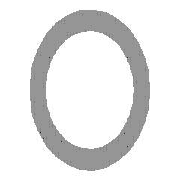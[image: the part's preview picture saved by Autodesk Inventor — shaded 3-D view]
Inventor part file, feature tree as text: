
AUTODESK INVENTOR PART (.ipt)
format: ipt  version: 2013 (Build 170138000, 138)  size: 109,568 bytes
history: native  units: mm (DEFAULTED — no unit token found)
features: other x4, sketch x3, plane x1
ambient origin geometry x8: Origin, YZ Plane, XZ Plane, XY Plane, X Axis, Y Axis, Z Axis, Center Point
bodies: Solid1 (feature_tree), Body (feature_tree)
feature tree (8):
  parser-record x1  (decoder bookkeeping rows leaked as tree rows — omitted from the tree; the rows remain in map.json)
  other  "Driven Length"
  other  "Start plane"
  other  "End plane"
  sketch  "Sketch"  dims[d2=365.252mm d3=0.0mm d4=-0.0mm d5=365.252mm d6=90.0deg d7=365.252mm]
  sketch  "Sketch3"  dims[d0=42.164mm]
  plane  "Work Plane3"
  sketch  "Sketch4"  dims[d1=3.556mm]
